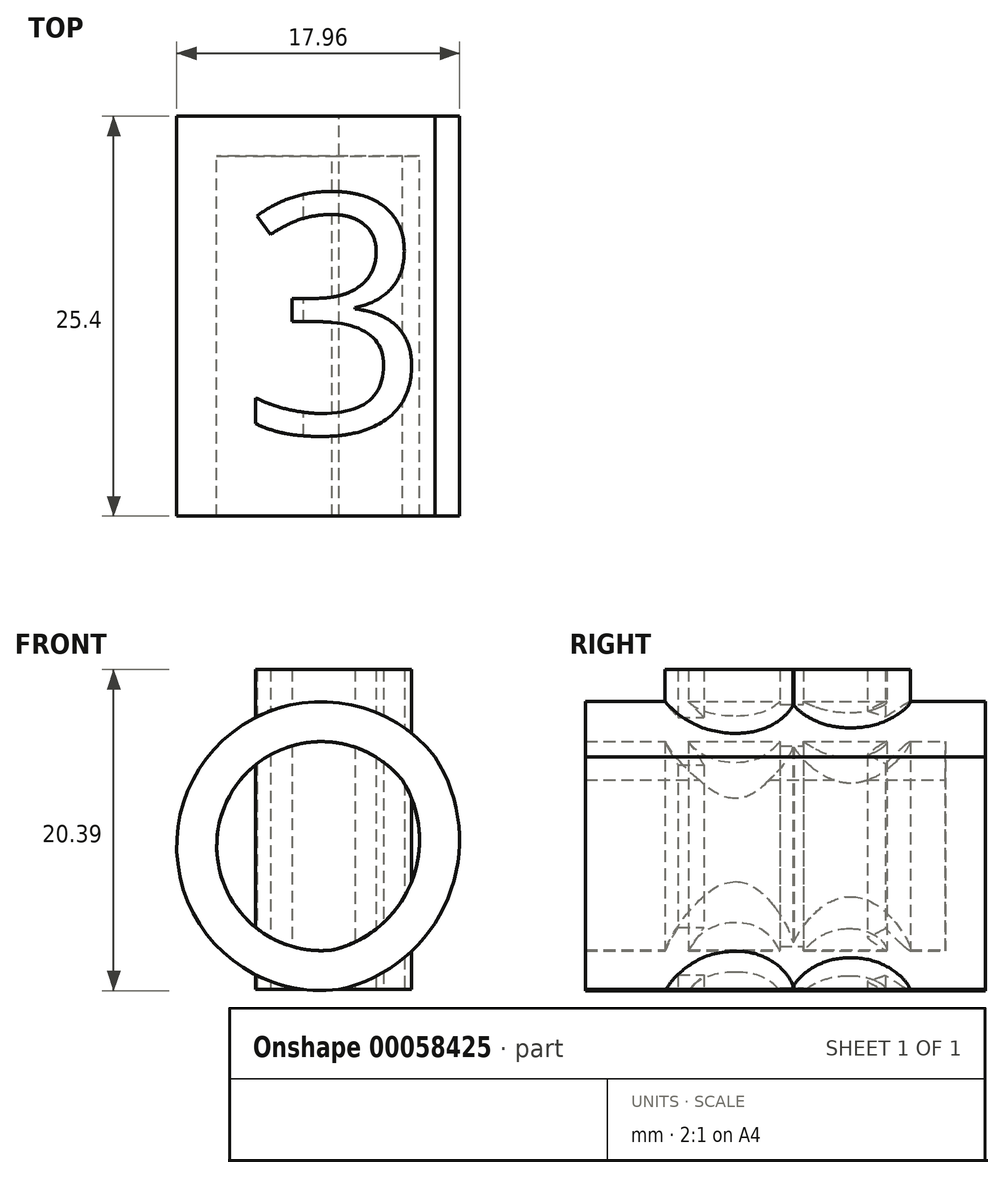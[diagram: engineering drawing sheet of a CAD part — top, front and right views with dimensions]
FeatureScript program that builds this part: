
annotation { "Feature Type Name" : "Feature", "Feature Type Description" : "" }
export const myFeature = defineFeature(function(context is Context, id is Id, definition is map)
    precondition{}
    {
        {
            var Q0;
            Q0=qCreatedBy(makeId("Front.planeOp"),FACE);
            var sketch = newSketch(context, id + "F0", { "sketchPlane" : qUnion([Q0])});
            skArc(sketch, "E0", {"start": v(6.1, 14.78) * mm, "mid": v(-9.6, 12.61) * mm, "end": v(0, 0) * mm});
            skArc(sketch, "E1", {"start": v(0, 0) * mm, "mid": v(6.93, 5.79) * mm, "end": v(6.1, 14.78) * mm});
            skSolve(sketch);
        }
        {
            var Q0;
            Q0=makeQuery(id+"F0.imprint","IMPRINT",FACE,{"disambiguationData":[TD([[makeQuery(id+"F0.imprint","IMPRINT",EDGE,{"derivedFrom":sQuery(id+"F0.wireOp",EDGE,"E0")}),1.0]])]});
            extrude(context, id + "F1", {"entities" : qUnion([Q0]), "depth" : 25.4 * mm});
        }
        {
            var Q0;
            Q0=makeQuery(id+"F1.opExtrude","CAP_FACE",FACE,{"disambiguationData":[OSD([sQuery(id+"F0.wireOp",EDGE,"E0"),sQuery(id+"F0.wireOp",EDGE,"E1")])],"isStart":false});
            shell(context, id + "F2", {"entities" : qUnion([Q0]), "thickness" : 2.54 * mm});
        }
        {
            var Q0;
            Q0=makeQuery(id+"F1.opExtrude","CAP_FACE",FACE,{"disambiguationData":[OSD([sQuery(id+"F0.wireOp",EDGE,"E0"),sQuery(id+"F0.wireOp",EDGE,"E1")])],"isStart":false});
            var sketch = newSketch(context, id + "F3", { "sketchPlane" : qUnion([Q0])});
            skSolve(sketch);
        }
        {
            var Q0;
            {var subQ0=sQuery(id+"F0.wireOp",EDGE,"E0");var subQ1=makeQuery(id+"F1.opExtrude","CAP_EDGE",EDGE,{"disambiguationData":[OSD([subQ0])],"isStart":false});Q0=makeQuery(id+"F3.imprint","IMPRINT",FACE,{"disambiguationData":[TD([[makeQuery(id+"F3.imprint","IMPRINT",EDGE,{"derivedFrom":subQ1}),1.0]])]});}
            var sketch = newSketch(context, id + "F4", { "sketchPlane" : qUnion([Q0])});
            skLineSegment(sketch, "E2.bottom", {"start": v(-2.06, 17.58) * mm, "end": v(0, 17.58) * mm});
            skLineSegment(sketch, "E2.top", {"start": v(-2.06, 16.32) * mm, "end": v(0, 16.32) * mm});
            skLineSegment(sketch, "E2.left", {"start": v(-2.06, 17.58) * mm, "end": v(-2.06, 16.32) * mm});
            skLineSegment(sketch, "E2.right", {"start": v(0, 17.58) * mm, "end": v(0, 16.32) * mm});
            skLineSegment(sketch, "E3.top", {"start": v(-2.33, 0.75) * mm, "end": v(-0.27, 0.75) * mm});
            skLineSegment(sketch, "E3.right", {"start": v(-0.27, 2) * mm, "end": v(-0.27, 0.75) * mm});
            skLineSegment(sketch, "E3.bottom", {"start": v(-2.33, 2) * mm, "end": v(-0.27, 2) * mm});
            skLineSegment(sketch, "E3.left", {"start": v(-2.33, 2) * mm, "end": v(-2.33, 0.75) * mm});
            skSolve(sketch);
        }
        {
            var Q0;
            Q0=sQuery(id+"F4.wireOp",EDGE,"E2.top");
            var Q1;
            Q1=sQuery(id+"F4.wireOp",EDGE,"E2.right");
            var Q2;
            Q2=sQuery(id+"F4.wireOp",EDGE,"E2.left");
            var Q3;
            Q3=sQuery(id+"F4.wireOp",EDGE,"E3.left");
            var Q4;
            Q4=sQuery(id+"F4.wireOp",EDGE,"E3.right");
            var Q5;
            Q5=sQuery(id+"F4.wireOp",EDGE,"E3.top");
            var Q6;
            Q6=sQuery(id+"F4.wireOp",EDGE,"E3.bottom");
            var Q7;
            Q7=qConstructionFilter(qBodyType(qCreatedBy(id+"F3",EDGE),BodyType.WIRE),ConstructionObject.NO);
            var Q8;
            Q8=sQuery(id+"F4.wireOp",EDGE,"E2.bottom");
            extrude(context, id + "F5", {"bodyType" : ToolBodyType.SURFACE, "surfaceEntities" : qUnion([Q0, Q1, Q2, Q3, Q4, Q5, Q6, Q7, Q8]), "depth" : 3.17 * mm});
        }
        {
            var Q0;
            Q0=qCreatedBy(makeId("Top.planeOp"),FACE);
            var sketch = newSketch(context, id + "F6", { "sketchPlane" : qUnion([Q0])});
            skText(sketch, "E4", { "text": "3", "fontName": "OpenSans-Regular.ttf"});
            const initialGuessF6  = {"E4": [-0.00626, -0.02013, 1, 0, 0.01527]};
            skSetInitialGuess(sketch, initialGuessF6);
            skSolve(sketch);
        }
        {
            var Q0;
            Q0 = qSketchRegion(id + "F6", true);
            extrude(context, id + "F7", {"entities" : qUnion([Q0]), "operationType" : NewBodyOperationType.ADD, "depth" : 20.32 * mm});
        }
    });
